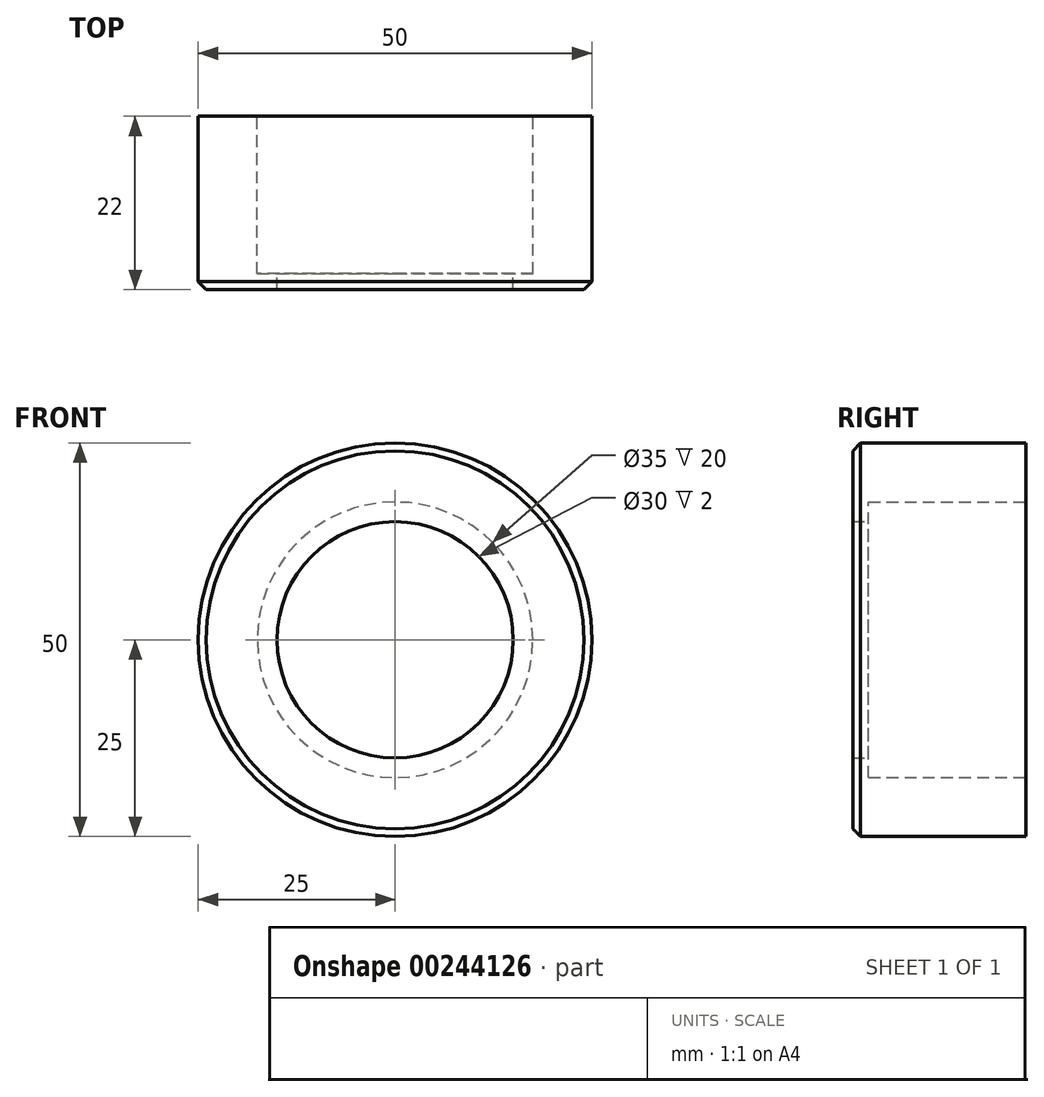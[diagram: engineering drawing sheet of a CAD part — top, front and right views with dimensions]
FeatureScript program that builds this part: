
annotation { "Feature Type Name" : "Feature", "Feature Type Description" : "" }
export const myFeature = defineFeature(function(context is Context, id is Id, definition is map)
    precondition{}
    {
        {
            var Q0;
            Q0=qCreatedBy(makeId("Front.planeOp"),FACE);
            var sketch = newSketch(context, id + "F0", { "sketchPlane" : qUnion([Q0])});
            skCircle(sketch, "E0", {"center": v(0, 0) * mm, "radius": 25 * mm});
            skCircle(sketch, "E1", {"center": v(0, 0) * mm, "radius": 17.5 * mm});
            skSolve(sketch);
        }
        {
            var Q0;
            Q0=makeQuery(id+"F0.imprint","IMPRINT",FACE,{"disambiguationData":[TD([[makeQuery(id+"F0.imprint","IMPRINT",EDGE,{"derivedFrom":sQuery(id+"F0.wireOp",EDGE,"E0")}),1.0]])]});
            extrude(context, id + "F1", {"entities" : qUnion([Q0]), "depth" : 20 * mm});
        }
        {
            var Q0;
            Q0=makeQuery(id+"F1.opExtrude","CAP_FACE",FACE,{"disambiguationData":[OSD([sQuery(id+"F0.wireOp",EDGE,"E0"),sQuery(id+"F0.wireOp",EDGE,"E1")])],"isStart":false});
            var sketch = newSketch(context, id + "F2", { "sketchPlane" : qUnion([Q0])});
            skCircle(sketch, "E2", {"center": v(0, 0) * mm, "radius": 25 * mm});
            skCircle(sketch, "E3", {"center": v(0, 0) * mm, "radius": 15 * mm});
            skSolve(sketch);
        }
        {
            var Q0;
            Q0 = qSketchRegion(id + "F2", true);
            extrude(context, id + "F3", {"entities" : qUnion([Q0]), "operationType" : NewBodyOperationType.ADD, "depth" : 2 * mm});
        }
        {
            var Q0;
            Q0=makeQuery(id+"F3.opExtrude","CAP_EDGE",EDGE,{"disambiguationData":[OSD([sQuery(id+"F2.wireOp",EDGE,"E2")])],"isStart":false});
            chamfer(context, id + "F4", {"entities" : qUnion([Q0]), "width" : 1 * mm, "tangentPropagation" : true});
        }
    });
